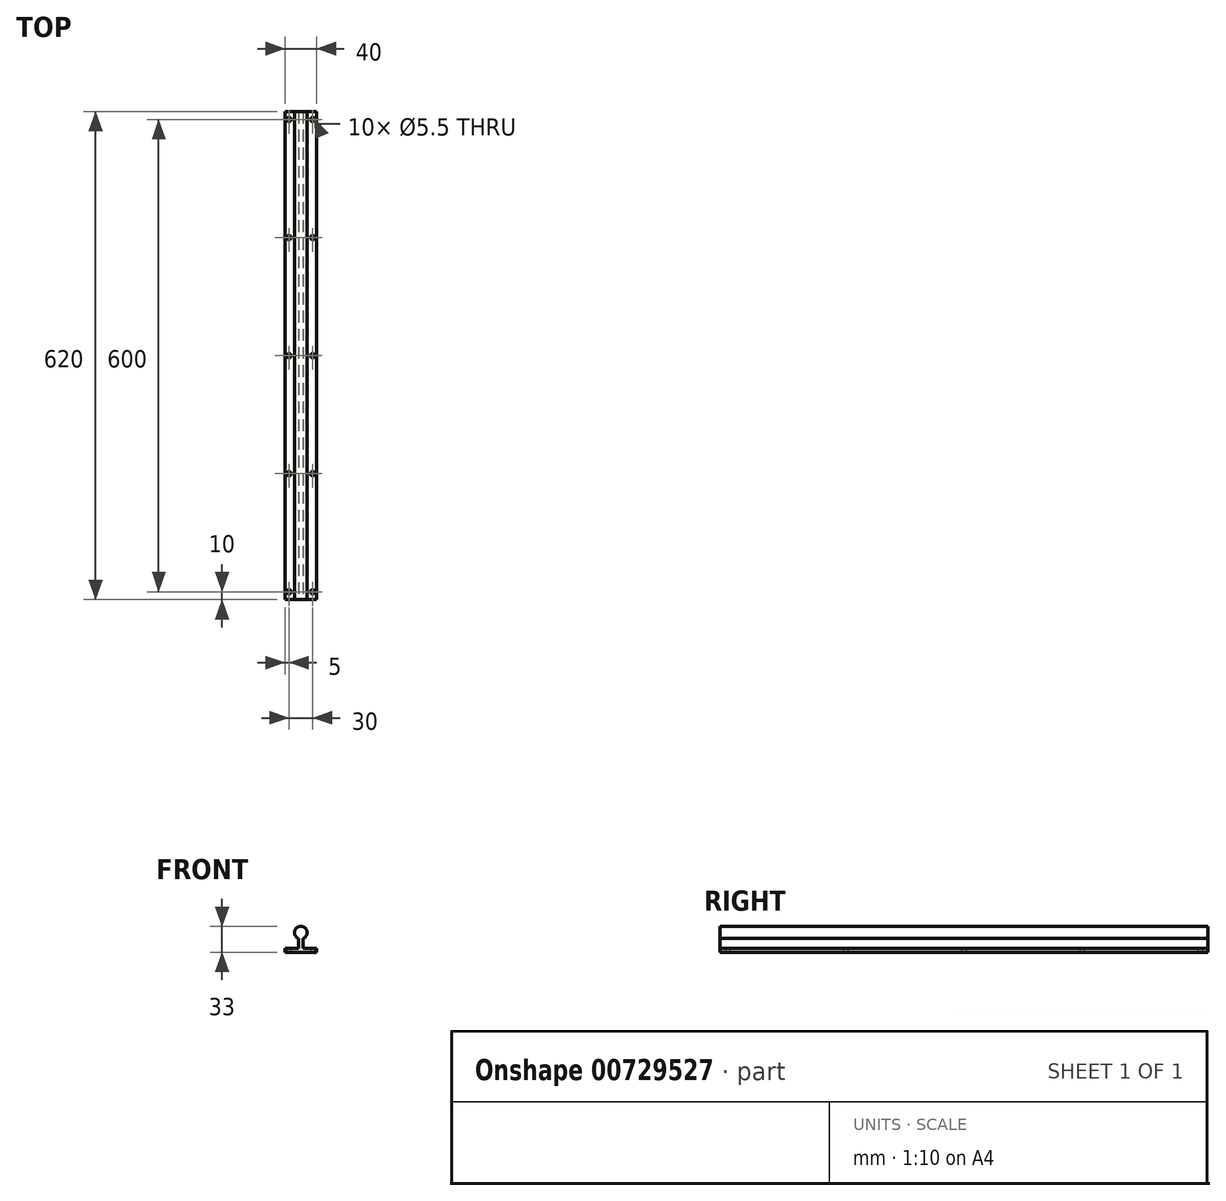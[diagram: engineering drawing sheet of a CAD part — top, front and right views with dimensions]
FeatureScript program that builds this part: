
annotation { "Feature Type Name" : "Feature", "Feature Type Description" : "" }
export const myFeature = defineFeature(function(context is Context, id is Id, definition is map)
    precondition{}
    {
        {
            var Q0;
            Q0=qCreatedBy(makeId("Front.planeOp"),FACE);
            var sketch = newSketch(context, id + "F0", { "sketchPlane" : qUnion([Q0])});
            skLineSegment(sketch, "E0.bottom", {"start": v(20, 2.5) * mm, "end": v(3, 2.5) * mm});
            skLineSegment(sketch, "E0.top", {"start": v(20, -2.5) * mm, "end": v(-20, -2.5) * mm});
            skLineSegment(sketch, "E0.left", {"start": v(20, 2.5) * mm, "end": v(20, -2.5) * mm});
            skLineSegment(sketch, "E0.right", {"start": v(-20, 2.5) * mm, "end": v(-20, -2.5) * mm});
            skPoint(sketch, "E0.middle", {"position": v(0, 0) * mm});
            skLineSegment(sketch, "E1.left", {"start": v(-3, 2.5) * mm, "end": v(-3, 15.08) * mm});
            skLineSegment(sketch, "E1.right", {"start": v(3, 2.5) * mm, "end": v(3, 15.08) * mm});
            skLineSegment(sketch, "E2", {"start": v(0, 50.09) * mm, "end": v(0, -27) * mm, "construction": true});
            skArc(sketch, "E3", {"start": v(3, 15.08) * mm, "mid": v(0, 30.5) * mm, "end": v(-3, 15.08) * mm});
            skLineSegment(sketch, "E4.trimOffspring", {"start": v(-3, 2.5) * mm, "end": v(-20, 2.5) * mm});
            skSolve(sketch);
        }
        {
            var Q0;
            Q0=qCreatedBy(makeId("Top.planeOp"),FACE);
            var sketch = newSketch(context, id + "F1", { "sketchPlane" : qUnion([Q0])});
            skLineSegment(sketch, "E5", {"start": v(-20, 0) * mm, "end": v(-20, 620) * mm});
            skLineSegment(sketch, "E6", {"start": v(-20, 620) * mm, "end": v(20, 620) * mm});
            skLineSegment(sketch, "E7", {"start": v(20, 620) * mm, "end": v(20, 0) * mm});
            skLineSegment(sketch, "E8", {"start": v(15, 2225.2) * mm, "end": v(15, -705.2) * mm, "construction": true});
            skCircle(sketch, "E9", {"center": v(15, 10) * mm, "radius": 2.75 * mm});
            skCircle(sketch, "E10", {"center": v(15, 160) * mm, "radius": 2.75 * mm});
            skCircle(sketch, "E11", {"center": v(15, 310) * mm, "radius": 2.75 * mm});
            skCircle(sketch, "E12", {"center": v(15, 460) * mm, "radius": 2.75 * mm});
            skCircle(sketch, "E13", {"center": v(15, 610) * mm, "radius": 2.75 * mm});
            skLineSegment(sketch, "E14", {"start": v(0, 654.2) * mm, "end": v(0, 0) * mm, "construction": true});
            skLineSegment(sketch, "E15.MirrorCS", {"start": v(-15, 2225.2) * mm, "end": v(-15, -705.2) * mm, "construction": true});
            skCircle(sketch, "E16.MirrorC", {"center": v(-15, 10) * mm, "radius": 2.75 * mm});
            skCircle(sketch, "E17.MirrorC", {"center": v(-15, 160) * mm, "radius": 2.75 * mm});
            skCircle(sketch, "E18.MirrorC", {"center": v(-15, 310) * mm, "radius": 2.75 * mm});
            skCircle(sketch, "E19.MirrorC", {"center": v(-15, 460) * mm, "radius": 2.75 * mm});
            skCircle(sketch, "E20.MirrorC", {"center": v(-15, 610) * mm, "radius": 2.75 * mm});
            skSolve(sketch);
        }
        {
            var Q0;
            Q0 = qSketchRegion(id + "F0", true);
            extrude(context, id + "F2", {"entities" : qUnion([Q0]), "oppositeDirection" : true, "depth" : 620 * mm, "offsetDistance" : 25 * mm});
        }
        {
            var Q0;
            Q0 = qSketchRegion(id + "F1", true);
            extrude(context, id + "F3", {"entities" : qUnion([Q0]), "operationType" : NewBodyOperationType.REMOVE, "depth" : 5.5 * mm, "offsetDistance" : 25 * mm, "symmetric" : true});
        }
    });
